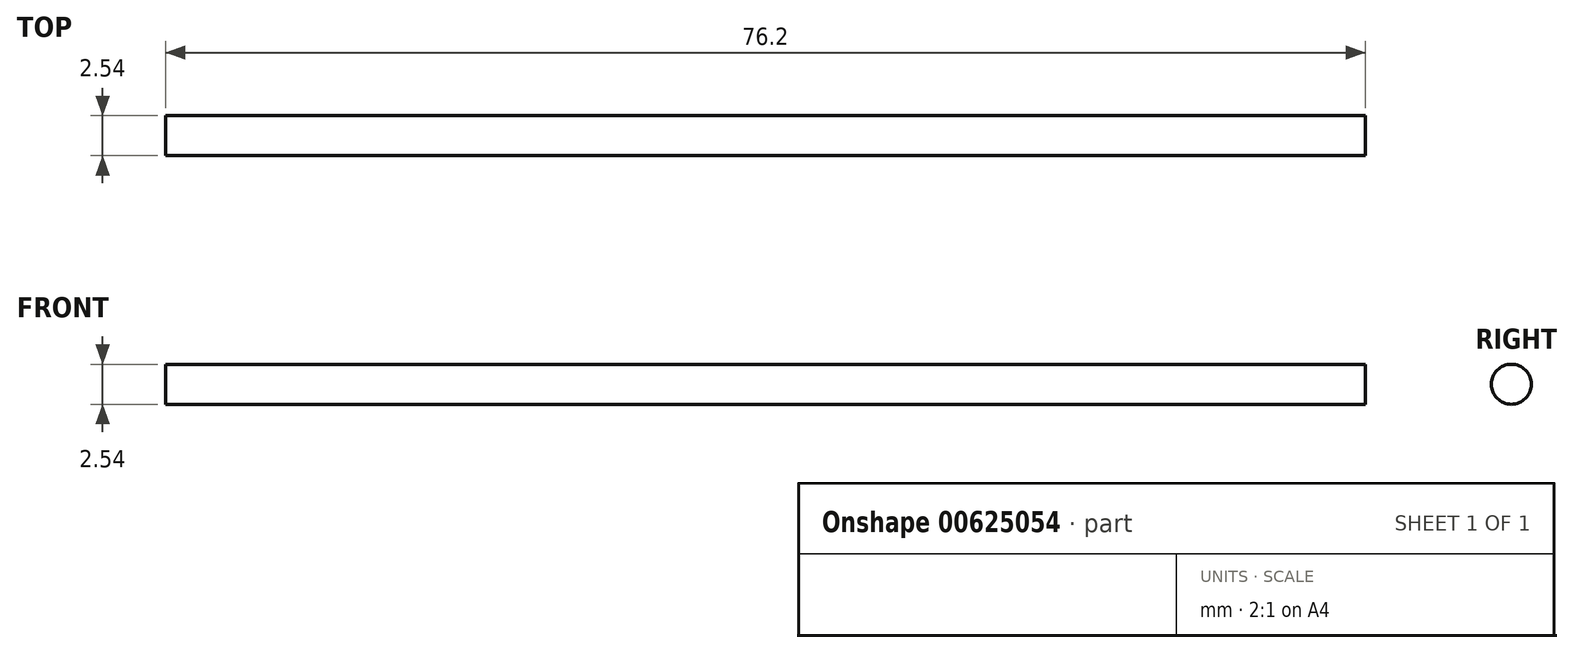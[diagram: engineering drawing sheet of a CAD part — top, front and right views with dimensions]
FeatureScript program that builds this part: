
annotation { "Feature Type Name" : "Feature", "Feature Type Description" : "" }
export const myFeature = defineFeature(function(context is Context, id is Id, definition is map)
    precondition{}
    {
        {
            var Q0;
            Q0=qCreatedBy(makeId("Right.planeOp"),FACE);
            var sketch = newSketch(context, id + "F0", { "sketchPlane" : qUnion([Q0])});
            skCircle(sketch, "E0", {"center": v(0, 0) * mm, "radius": 1.27 * mm});
            skSolve(sketch);
        }
        {
            var Q0;
            Q0=sQuery(id+"F0.wireOp",EDGE,"E0");
            extrude(context, id + "F1", {"bodyType" : ToolBodyType.SURFACE, "surfaceEntities" : qUnion([Q0]), "depth" : 76.2 * mm, "offsetDistance" : 25.4 * mm});
        }
    });
